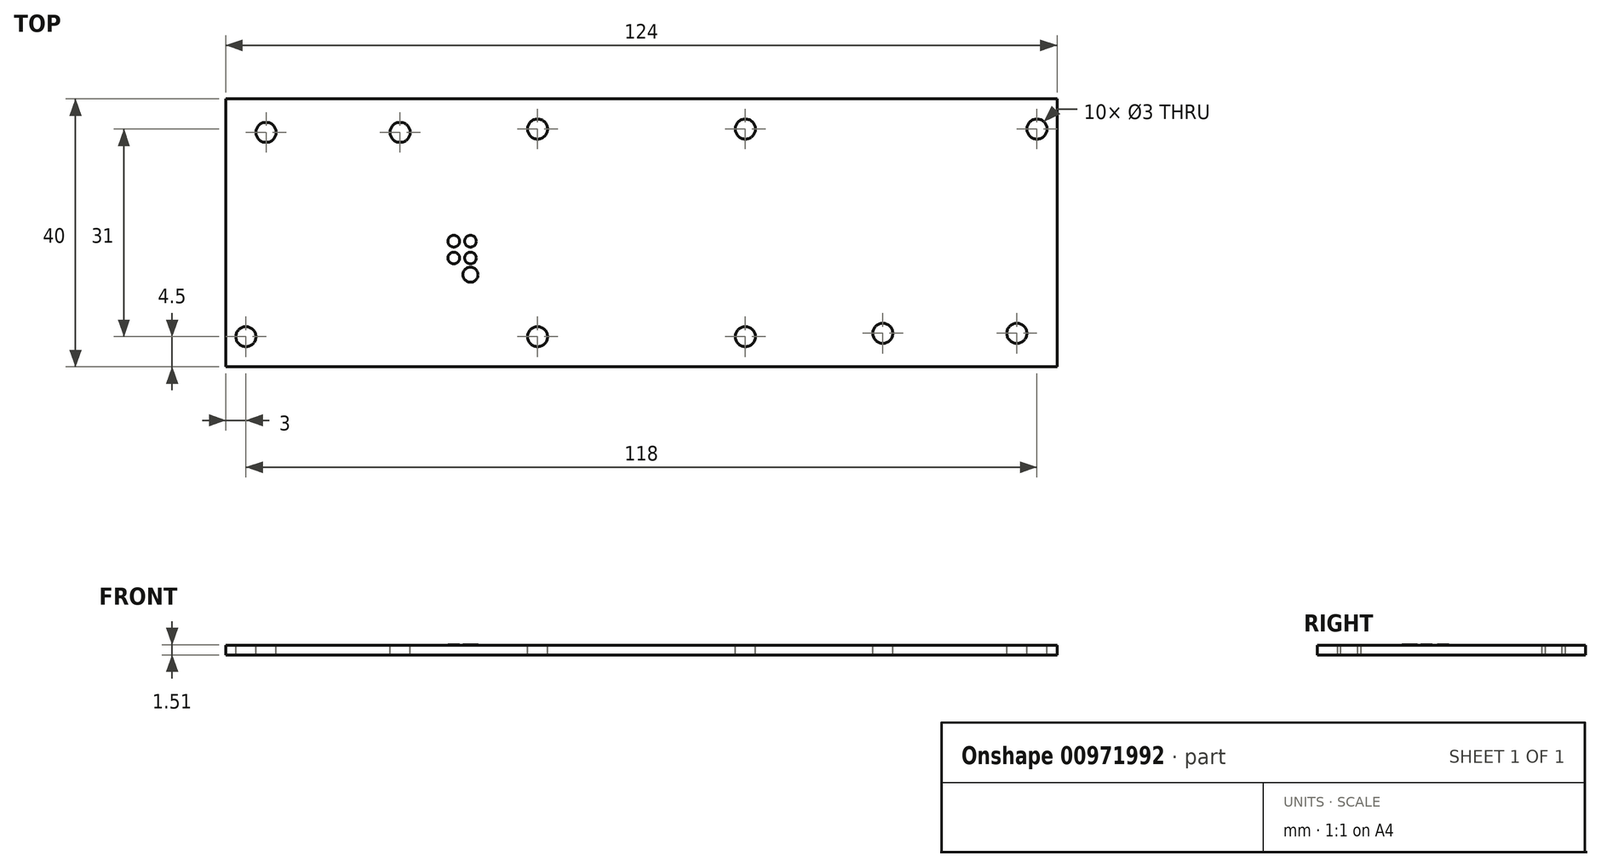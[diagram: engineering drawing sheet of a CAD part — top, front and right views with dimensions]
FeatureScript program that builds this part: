
annotation { "Feature Type Name" : "Feature", "Feature Type Description" : "" }
export const myFeature = defineFeature(function(context is Context, id is Id, definition is map)
    precondition{}
    {
        {
            var Q0;
            Q0=qCreatedBy(makeId("Top.planeOp"),FACE);
            var sketch = newSketch(context, id + "F0", { "sketchPlane" : qUnion([Q0])});
            skLineSegment(sketch, "E0.bottom", {"start": v(-62, 20) * mm, "end": v(62, 20) * mm});
            skLineSegment(sketch, "E0.top", {"start": v(-62, -20) * mm, "end": v(62, -20) * mm});
            skLineSegment(sketch, "E0.left", {"start": v(-62, 20) * mm, "end": v(-62, -20) * mm});
            skLineSegment(sketch, "E0.right", {"start": v(62, 20) * mm, "end": v(62, -20) * mm});
            skPoint(sketch, "E0.middle", {"position": v(0, 0) * mm});
            skSolve(sketch);
        }
        {
            var Q0;
            Q0=makeQuery(id+"F0.imprint","IMPRINT",FACE,{"disambiguationData":[TD([[makeQuery(id+"F0.imprint","IMPRINT",EDGE,{"derivedFrom":sQuery(id+"F0.wireOp",EDGE,"E0.bottom")}),-1.0]])]});
            extrude(context, id + "F1", {"entities" : qUnion([Q0]), "depth" : 1.41 * mm, "offsetDistance" : 25 * mm});
        }
        {
            var Q0;
            Q0=makeQuery(id+"F1.opExtrude","CAP_FACE",FACE,{"disambiguationData":[OSD([sQuery(id+"F0.wireOp",EDGE,"E0.bottom"),sQuery(id+"F0.wireOp",EDGE,"E0.top"),sQuery(id+"F0.wireOp",EDGE,"E0.left"),sQuery(id+"F0.wireOp",EDGE,"E0.right")])],"isStart":false});
            var sketch = newSketch(context, id + "F2", { "sketchPlane" : qUnion([Q0])});
            skLineSegment(sketch, "E1.bottom", {"start": v(-62, 18.5) * mm, "end": v(62, 18.5) * mm});
            skLineSegment(sketch, "E1.top", {"start": v(-62, -18.5) * mm, "end": v(62, -18.5) * mm});
            skLineSegment(sketch, "E1.left", {"start": v(-62, 18.5) * mm, "end": v(-62, -18.5) * mm});
            skLineSegment(sketch, "E1.right", {"start": v(62, 18.5) * mm, "end": v(62, -18.5) * mm});
            skPoint(sketch, "E1.middle", {"position": v(0, 0) * mm});
            skLineSegment(sketch, "E2.bottom", {"start": v(-62, -18.5) * mm, "end": v(-59, -18.5) * mm});
            skLineSegment(sketch, "E2.top", {"start": v(-62, -15.5) * mm, "end": v(-59, -15.5) * mm});
            skLineSegment(sketch, "E2.left", {"start": v(-62, -18.5) * mm, "end": v(-62, -15.5) * mm});
            skLineSegment(sketch, "E2.right", {"start": v(-59, -18.5) * mm, "end": v(-59, -15.5) * mm});
            skLineSegment(sketch, "E3.bottom", {"start": v(-62, 18.5) * mm, "end": v(-56, 18.5) * mm});
            skLineSegment(sketch, "E3.top", {"start": v(-62, 15) * mm, "end": v(-56, 15) * mm});
            skLineSegment(sketch, "E3.left", {"start": v(-62, 18.5) * mm, "end": v(-62, 15) * mm});
            skLineSegment(sketch, "E3.right", {"start": v(-56, 18.5) * mm, "end": v(-56, 15) * mm});
            skLineSegment(sketch, "E4", {"start": v(-59, -15.5) * mm, "end": v(-59, 15) * mm});
            skLineSegment(sketch, "E5", {"start": v(-56, 15) * mm, "end": v(-36, 15) * mm});
            skCircle(sketch, "E6", {"center": v(-56, 15) * mm, "radius": 1.5 * mm});
            skCircle(sketch, "E7", {"center": v(-59, -15.5) * mm, "radius": 1.5 * mm});
            skCircle(sketch, "E8", {"center": v(-36, 15) * mm, "radius": 1.5 * mm});
            skLineSegment(sketch, "E9.bottom", {"start": v(62, 18.5) * mm, "end": v(59, 18.5) * mm});
            skLineSegment(sketch, "E9.top", {"start": v(62, 15.5) * mm, "end": v(59, 15.5) * mm});
            skLineSegment(sketch, "E9.left", {"start": v(62, 18.5) * mm, "end": v(62, 15.5) * mm});
            skLineSegment(sketch, "E9.right", {"start": v(59, 18.5) * mm, "end": v(59, 15.5) * mm});
            skLineSegment(sketch, "E10", {"start": v(59, 15.5) * mm, "end": v(59, -15) * mm});
            skLineSegment(sketch, "E11", {"start": v(59, -15) * mm, "end": v(56, -15) * mm});
            skCircle(sketch, "E12", {"center": v(56, -15) * mm, "radius": 1.5 * mm});
            skLineSegment(sketch, "E13", {"start": v(56, -15) * mm, "end": v(36, -15) * mm});
            skCircle(sketch, "E14", {"center": v(36, -15) * mm, "radius": 1.5 * mm});
            skCircle(sketch, "E15", {"center": v(59, 15.5) * mm, "radius": 1.5 * mm});
            skSolve(sketch);
        }
        {
            var Q0;
            {var subQ0=sQuery(id+"F2.wireOp",EDGE,"E5");var subQ3=sQuery(id+"F2.wireOp",EDGE,"E6");var subQ5=makeQuery(id+"F2.imprint","INTERSECT",VERTEX,{"derivedFrom":[subQ0,subQ3]});Q0=makeQuery(id+"F2.imprint","IMPRINT",FACE,{"disambiguationData":[TD([[makeQuery(id+"F2.imprint","IMPRINT",EDGE,{"disambiguationData":[TD([[subQ5,1.0]])],"derivedFrom":subQ3}),1.0]])]});}
            var Q1;
            {var subQ1=sQuery(id+"F2.wireOp",EDGE,"E3.top");var subQ3=sQuery(id+"F2.wireOp",EDGE,"E6");var subQ4=makeQuery(id+"F2.imprint","INTERSECT",VERTEX,{"derivedFrom":[subQ1,subQ3]});Q1=makeQuery(id+"F2.imprint","IMPRINT",FACE,{"disambiguationData":[TD([[makeQuery(id+"F2.imprint","IMPRINT",EDGE,{"disambiguationData":[TD([[subQ4,1.0]])],"derivedFrom":subQ3}),1.0]])]});}
            var Q2;
            {var subQ0=sQuery(id+"F2.wireOp",EDGE,"E5");var subQ3=sQuery(id+"F2.wireOp",EDGE,"E6");var subQ5=makeQuery(id+"F2.imprint","INTERSECT",VERTEX,{"derivedFrom":[subQ0,subQ3]});Q2=makeQuery(id+"F2.imprint","IMPRINT",FACE,{"disambiguationData":[TD([[makeQuery(id+"F2.imprint","IMPRINT",EDGE,{"disambiguationData":[TD([[subQ5,-1.0]])],"derivedFrom":subQ3}),1.0]])]});}
            var Q3;
            Q3=makeQuery(id+"F2.imprint","IMPRINT",FACE,{"disambiguationData":[TD([[makeQuery(id+"F2.imprint","IMPRINT",EDGE,{"derivedFrom":sQuery(id+"F2.wireOp",EDGE,"E8")}),1.0]])]});
            var Q4;
            {var subQ1=sQuery(id+"F2.wireOp",EDGE,"E2.right");var subQ3=sQuery(id+"F2.wireOp",EDGE,"E7");var subQ4=makeQuery(id+"F2.imprint","INTERSECT",VERTEX,{"derivedFrom":[subQ1,subQ3]});Q4=makeQuery(id+"F2.imprint","IMPRINT",FACE,{"disambiguationData":[TD([[makeQuery(id+"F2.imprint","IMPRINT",EDGE,{"disambiguationData":[TD([[subQ4,-1.0]])],"derivedFrom":subQ3}),1.0]])]});}
            var Q5;
            {var subQ1=sQuery(id+"F2.wireOp",EDGE,"E2.top");var subQ3=sQuery(id+"F2.wireOp",EDGE,"E7");var subQ4=makeQuery(id+"F2.imprint","INTERSECT",VERTEX,{"derivedFrom":[subQ1,subQ3]});Q5=makeQuery(id+"F2.imprint","IMPRINT",FACE,{"disambiguationData":[TD([[makeQuery(id+"F2.imprint","IMPRINT",EDGE,{"disambiguationData":[TD([[subQ4,1.0]])],"derivedFrom":subQ3}),1.0]])]});}
            var Q6;
            {var subQ1=sQuery(id+"F2.wireOp",EDGE,"E2.top");var subQ3=sQuery(id+"F2.wireOp",EDGE,"E7");var subQ4=makeQuery(id+"F2.imprint","INTERSECT",VERTEX,{"derivedFrom":[subQ1,subQ3]});Q6=makeQuery(id+"F2.imprint","IMPRINT",FACE,{"disambiguationData":[TD([[makeQuery(id+"F2.imprint","IMPRINT",EDGE,{"disambiguationData":[TD([[subQ4,-1.0]])],"derivedFrom":subQ3}),1.0]])]});}
            var Q7;
            {var subQ1=sQuery(id+"F2.wireOp",EDGE,"E9.top");var subQ3=sQuery(id+"F2.wireOp",EDGE,"E15");var subQ4=makeQuery(id+"F2.imprint","INTERSECT",VERTEX,{"derivedFrom":[subQ1,subQ3]});Q7=makeQuery(id+"F2.imprint","IMPRINT",FACE,{"disambiguationData":[TD([[makeQuery(id+"F2.imprint","IMPRINT",EDGE,{"disambiguationData":[TD([[subQ4,-1.0]])],"derivedFrom":subQ3}),1.0]])]});}
            var Q8;
            {var subQ0=sQuery(id+"F2.wireOp",EDGE,"E10");var subQ3=sQuery(id+"F2.wireOp",EDGE,"E15");var subQ5=makeQuery(id+"F2.imprint","INTERSECT",VERTEX,{"derivedFrom":[subQ0,subQ3]});Q8=makeQuery(id+"F2.imprint","IMPRINT",FACE,{"disambiguationData":[TD([[makeQuery(id+"F2.imprint","IMPRINT",EDGE,{"disambiguationData":[TD([[subQ5,-1.0]])],"derivedFrom":subQ3}),1.0]])]});}
            var Q9;
            {var subQ0=sQuery(id+"F2.wireOp",EDGE,"E10");var subQ3=sQuery(id+"F2.wireOp",EDGE,"E15");var subQ5=makeQuery(id+"F2.imprint","INTERSECT",VERTEX,{"derivedFrom":[subQ0,subQ3]});Q9=makeQuery(id+"F2.imprint","IMPRINT",FACE,{"disambiguationData":[TD([[makeQuery(id+"F2.imprint","IMPRINT",EDGE,{"disambiguationData":[TD([[subQ5,1.0]])],"derivedFrom":subQ3}),1.0]])]});}
            var Q10;
            {var subQ0=sQuery(id+"F2.wireOp",EDGE,"E13");var subQ1=sQuery(id+"F2.wireOp",EDGE,"E11");var subQ2=makeQuery(id+"F2.imprint","INTERSECT",VERTEX,{"derivedFrom":[subQ1,subQ0]});Q10=makeQuery(id+"F2.imprint","IMPRINT",FACE,{"disambiguationData":[TD([[makeQuery(id+"F2.imprint","IMPRINT",EDGE,{"disambiguationData":[TD([[subQ2,1.0]])],"derivedFrom":subQ1}),1.0]])]});}
            var Q11;
            {var subQ0=sQuery(id+"F2.wireOp",EDGE,"E13");var subQ1=sQuery(id+"F2.wireOp",EDGE,"E11");var subQ2=makeQuery(id+"F2.imprint","INTERSECT",VERTEX,{"derivedFrom":[subQ1,subQ0]});Q11=makeQuery(id+"F2.imprint","IMPRINT",FACE,{"disambiguationData":[TD([[makeQuery(id+"F2.imprint","IMPRINT",EDGE,{"disambiguationData":[TD([[subQ2,1.0]])],"derivedFrom":subQ1}),-1.0]])]});}
            var Q12;
            Q12=makeQuery(id+"F2.imprint","IMPRINT",FACE,{"disambiguationData":[TD([[makeQuery(id+"F2.imprint","IMPRINT",EDGE,{"derivedFrom":sQuery(id+"F2.wireOp",EDGE,"E14")}),1.0]])]});
            extrude(context, id + "F3", {"entities" : qUnion([Q0, Q1, Q2, Q3, Q4, Q5, Q6, Q7, Q8, Q9, Q10, Q11, Q12]), "operationType" : NewBodyOperationType.REMOVE, "oppositeDirection" : true, "depth" : 25 * mm, "offsetDistance" : 25 * mm});
        }
        {
            var Q0;
            Q0=makeQuery(id+"F1.opExtrude","CAP_FACE",FACE,{"disambiguationData":[OSD([sQuery(id+"F0.wireOp",EDGE,"E0.bottom"),sQuery(id+"F0.wireOp",EDGE,"E0.top"),sQuery(id+"F0.wireOp",EDGE,"E0.left"),sQuery(id+"F0.wireOp",EDGE,"E0.right")])],"isStart":false});
            var sketch = newSketch(context, id + "F4", { "sketchPlane" : qUnion([Q0])});
            skLineSegment(sketch, "E16.bottom", {"start": v(-15.5, 15.5) * mm, "end": v(15.5, 15.5) * mm});
            skLineSegment(sketch, "E16.top", {"start": v(-15.5, -15.5) * mm, "end": v(15.5, -15.5) * mm});
            skLineSegment(sketch, "E16.left", {"start": v(-15.5, 15.5) * mm, "end": v(-15.5, -15.5) * mm});
            skLineSegment(sketch, "E16.right", {"start": v(15.5, 15.5) * mm, "end": v(15.5, -15.5) * mm});
            skPoint(sketch, "E16.middle", {"position": v(0, 0) * mm});
            skCircle(sketch, "E17", {"center": v(-15.5, 15.5) * mm, "radius": 1.5 * mm});
            skCircle(sketch, "E18", {"center": v(15.5, 15.5) * mm, "radius": 1.5 * mm});
            skCircle(sketch, "E19", {"center": v(15.5, -15.5) * mm, "radius": 1.5 * mm});
            skCircle(sketch, "E20", {"center": v(-15.5, -15.5) * mm, "radius": 1.5 * mm});
            skSolve(sketch);
        }
        {
            var Q0;
            {var subQ0=sQuery(id+"F4.wireOp",EDGE,"E16.left");var subQ1=sQuery(id+"F4.wireOp",EDGE,"E16.bottom");var subQ2=makeQuery(id+"F4.imprint","INTERSECT",VERTEX,{"derivedFrom":[subQ1,subQ0]});Q0=makeQuery(id+"F4.imprint","IMPRINT",FACE,{"disambiguationData":[TD([[makeQuery(id+"F4.imprint","IMPRINT",EDGE,{"disambiguationData":[TD([[subQ2,-1.0]])],"derivedFrom":subQ1}),1.0]])]});}
            var Q1;
            {var subQ0=sQuery(id+"F4.wireOp",EDGE,"E16.left");var subQ1=sQuery(id+"F4.wireOp",EDGE,"E16.bottom");var subQ2=makeQuery(id+"F4.imprint","INTERSECT",VERTEX,{"derivedFrom":[subQ1,subQ0]});Q1=makeQuery(id+"F4.imprint","IMPRINT",FACE,{"disambiguationData":[TD([[makeQuery(id+"F4.imprint","IMPRINT",EDGE,{"disambiguationData":[TD([[subQ2,-1.0]])],"derivedFrom":subQ1}),-1.0]])]});}
            var Q2;
            {var subQ0=sQuery(id+"F4.wireOp",EDGE,"E16.right");var subQ1=sQuery(id+"F4.wireOp",EDGE,"E16.bottom");var subQ2=makeQuery(id+"F4.imprint","INTERSECT",VERTEX,{"derivedFrom":[subQ1,subQ0]});Q2=makeQuery(id+"F4.imprint","IMPRINT",FACE,{"disambiguationData":[TD([[makeQuery(id+"F4.imprint","IMPRINT",EDGE,{"disambiguationData":[TD([[subQ2,1.0]])],"derivedFrom":subQ1}),-1.0]])]});}
            var Q3;
            {var subQ0=sQuery(id+"F4.wireOp",EDGE,"E16.right");var subQ1=sQuery(id+"F4.wireOp",EDGE,"E16.bottom");var subQ2=makeQuery(id+"F4.imprint","INTERSECT",VERTEX,{"derivedFrom":[subQ1,subQ0]});Q3=makeQuery(id+"F4.imprint","IMPRINT",FACE,{"disambiguationData":[TD([[makeQuery(id+"F4.imprint","IMPRINT",EDGE,{"disambiguationData":[TD([[subQ2,1.0]])],"derivedFrom":subQ1}),1.0]])]});}
            var Q4;
            {var subQ0=sQuery(id+"F4.wireOp",EDGE,"E16.left");var subQ1=sQuery(id+"F4.wireOp",EDGE,"E16.top");var subQ2=makeQuery(id+"F4.imprint","INTERSECT",VERTEX,{"derivedFrom":[subQ1,subQ0]});Q4=makeQuery(id+"F4.imprint","IMPRINT",FACE,{"disambiguationData":[TD([[makeQuery(id+"F4.imprint","IMPRINT",EDGE,{"disambiguationData":[TD([[subQ2,-1.0]])],"derivedFrom":subQ1}),1.0]])]});}
            var Q5;
            {var subQ0=sQuery(id+"F4.wireOp",EDGE,"E16.left");var subQ1=sQuery(id+"F4.wireOp",EDGE,"E16.top");var subQ2=makeQuery(id+"F4.imprint","INTERSECT",VERTEX,{"derivedFrom":[subQ1,subQ0]});Q5=makeQuery(id+"F4.imprint","IMPRINT",FACE,{"disambiguationData":[TD([[makeQuery(id+"F4.imprint","IMPRINT",EDGE,{"disambiguationData":[TD([[subQ2,-1.0]])],"derivedFrom":subQ1}),-1.0]])]});}
            var Q6;
            {var subQ0=sQuery(id+"F4.wireOp",EDGE,"E16.right");var subQ1=sQuery(id+"F4.wireOp",EDGE,"E16.top");var subQ2=makeQuery(id+"F4.imprint","INTERSECT",VERTEX,{"derivedFrom":[subQ1,subQ0]});Q6=makeQuery(id+"F4.imprint","IMPRINT",FACE,{"disambiguationData":[TD([[makeQuery(id+"F4.imprint","IMPRINT",EDGE,{"disambiguationData":[TD([[subQ2,1.0]])],"derivedFrom":subQ1}),1.0]])]});}
            var Q7;
            {var subQ0=sQuery(id+"F4.wireOp",EDGE,"E16.right");var subQ1=sQuery(id+"F4.wireOp",EDGE,"E16.top");var subQ2=makeQuery(id+"F4.imprint","INTERSECT",VERTEX,{"derivedFrom":[subQ1,subQ0]});Q7=makeQuery(id+"F4.imprint","IMPRINT",FACE,{"disambiguationData":[TD([[makeQuery(id+"F4.imprint","IMPRINT",EDGE,{"disambiguationData":[TD([[subQ2,1.0]])],"derivedFrom":subQ1}),-1.0]])]});}
            extrude(context, id + "F5", {"entities" : qUnion([Q0, Q1, Q2, Q3, Q4, Q5, Q6, Q7]), "operationType" : NewBodyOperationType.REMOVE, "oppositeDirection" : true, "depth" : 25 * mm, "offsetDistance" : 25 * mm});
        }
        {
            var Q0;
            Q0=makeQuery(id+"F1.opExtrude","CAP_FACE",FACE,{"disambiguationData":[OSD([sQuery(id+"F0.wireOp",EDGE,"E0.bottom"),sQuery(id+"F0.wireOp",EDGE,"E0.top"),sQuery(id+"F0.wireOp",EDGE,"E0.left"),sQuery(id+"F0.wireOp",EDGE,"E0.right")])],"isStart":false});
            var sketch = newSketch(context, id + "F6", { "sketchPlane" : qUnion([Q0])});
            skLineSegment(sketch, "E21", {"start": v(-62, -20) * mm, "end": v(-25.5, -20) * mm});
            skLineSegment(sketch, "E22", {"start": v(-25.5, -20) * mm, "end": v(-25.5, -6.25) * mm});
            skCircle(sketch, "E23", {"center": v(-25.5, -6.25) * mm, "radius": 1.13 * mm});
            skLineSegment(sketch, "E24", {"start": v(-25.5, -6.25) * mm, "end": v(-25.5, -3.75) * mm});
            skCircle(sketch, "E25", {"center": v(-25.5, -3.75) * mm, "radius": 0.88 * mm});
            skLineSegment(sketch, "E26", {"start": v(-25.5, -3.75) * mm, "end": v(-25.5, -1.25) * mm});
            skCircle(sketch, "E27", {"center": v(-25.5, -1.25) * mm, "radius": 0.88 * mm});
            skLineSegment(sketch, "E28.0", {"start": v(-62, 20) * mm, "end": v(-62, -20) * mm});
            skLineSegment(sketch, "E29", {"start": v(0, 0) * mm, "end": v(0, -18.5) * mm});
            skLineSegment(sketch, "E30", {"start": v(-25.5, -1.25) * mm, "end": v(-25.5, 1.25) * mm});
            skCircle(sketch, "E31", {"center": v(-25.5, 1.25) * mm, "radius": 1.13 * mm});
            skLineSegment(sketch, "E32", {"start": v(-25.5, 0.13) * mm, "end": v(-25.5, 1.25) * mm});
            skLineSegment(sketch, "E33", {"start": v(-20.67, 18.5) * mm, "end": v(-25.5, 18.5) * mm});
            skLineSegment(sketch, "E34", {"start": v(-25.5, 18.5) * mm, "end": v(-25.5, 18.38) * mm});
            skLineSegment(sketch, "E35.bottom", {"start": v(-25.5, -18.5) * mm, "end": v(25.5, -18.5) * mm});
            skLineSegment(sketch, "E35.top", {"start": v(-25.5, 18.5) * mm, "end": v(25.5, 18.5) * mm});
            skLineSegment(sketch, "E35.left", {"start": v(-25.5, -18.5) * mm, "end": v(-25.5, 18.5) * mm});
            skLineSegment(sketch, "E35.right", {"start": v(25.5, -18.5) * mm, "end": v(25.5, 18.5) * mm});
            skPoint(sketch, "E35.middle", {"position": v(0, 0) * mm});
            skLineSegment(sketch, "E36", {"start": v(-25.5, -1.25) * mm, "end": v(-28, -1.25) * mm});
            skCircle(sketch, "E37", {"center": v(-28, -1.25) * mm, "radius": 0.88 * mm});
            skCircle(sketch, "E38", {"center": v(-28, -3.75) * mm, "radius": 0.88 * mm});
            skLineSegment(sketch, "E39.trimOffspring", {"start": v(-25.5, 2.38) * mm, "end": v(-25.5, 18.38) * mm});
            skSolve(sketch);
        }
        {
            var Q0;
            Q0=makeQuery(id+"F6.imprint","IMPRINT",FACE,{"disambiguationData":[TD([[makeQuery(id+"F6.imprint","IMPRINT",EDGE,{"derivedFrom":sQuery(id+"F6.wireOp",EDGE,"E37")}),1.0]])]});
            var Q1;
            Q1=makeQuery(id+"F6.imprint","IMPRINT",FACE,{"disambiguationData":[TD([[makeQuery(id+"F6.imprint","IMPRINT",EDGE,{"derivedFrom":sQuery(id+"F6.wireOp",EDGE,"E38")}),1.0]])]});
            var Q2;
            {var subQ0=sQuery(id+"F6.wireOp",EDGE,"E35.left");var subQ1=sQuery(id+"F6.wireOp",EDGE,"E23");var subQ2=makeQuery(id+"F6.imprint","INTERSECT",VERTEX,{"disambiguationData":[OD(0.0)],"derivedFrom":[subQ1,subQ0]});Q2=makeQuery(id+"F6.imprint","IMPRINT",FACE,{"disambiguationData":[TD([[makeQuery(id+"F6.imprint","IMPRINT",EDGE,{"disambiguationData":[TD([[subQ2,1.0]])],"derivedFrom":subQ1}),1.0]])]});}
            var Q3;
            {var subQ0=sQuery(id+"F6.wireOp",EDGE,"E35.left");var subQ1=sQuery(id+"F6.wireOp",EDGE,"E23");var subQ2=makeQuery(id+"F6.imprint","INTERSECT",VERTEX,{"disambiguationData":[OD(0.0)],"derivedFrom":[subQ1,subQ0]});Q3=makeQuery(id+"F6.imprint","IMPRINT",FACE,{"disambiguationData":[TD([[makeQuery(id+"F6.imprint","IMPRINT",EDGE,{"disambiguationData":[TD([[subQ2,-1.0]])],"derivedFrom":subQ1}),1.0]])]});}
            var Q4;
            {var subQ0=sQuery(id+"F6.wireOp",EDGE,"E35.left");var subQ1=sQuery(id+"F6.wireOp",EDGE,"E25");var subQ2=makeQuery(id+"F6.imprint","INTERSECT",VERTEX,{"disambiguationData":[OD(0.0)],"derivedFrom":[subQ1,subQ0]});Q4=makeQuery(id+"F6.imprint","IMPRINT",FACE,{"disambiguationData":[TD([[makeQuery(id+"F6.imprint","IMPRINT",EDGE,{"disambiguationData":[TD([[subQ2,1.0]])],"derivedFrom":subQ1}),1.0]])]});}
            var Q5;
            {var subQ0=sQuery(id+"F6.wireOp",EDGE,"E35.left");var subQ1=sQuery(id+"F6.wireOp",EDGE,"E25");var subQ2=makeQuery(id+"F6.imprint","INTERSECT",VERTEX,{"disambiguationData":[OD(0.0)],"derivedFrom":[subQ1,subQ0]});Q5=makeQuery(id+"F6.imprint","IMPRINT",FACE,{"disambiguationData":[TD([[makeQuery(id+"F6.imprint","IMPRINT",EDGE,{"disambiguationData":[TD([[subQ2,-1.0]])],"derivedFrom":subQ1}),1.0]])]});}
            var Q6;
            {var subQ0=sQuery(id+"F6.wireOp",EDGE,"E35.left");var subQ4=makeQuery(id+"F6.imprint","IMPRINT",VERTEX,{"derivedFrom":subQ0});Q6=makeQuery(id+"F6.imprint","IMPRINT",FACE,{"disambiguationData":[TD([[makeQuery(id+"F6.imprint","IMPRINT",EDGE,{"disambiguationData":[TD([[subQ4,1.0]])],"derivedFrom":subQ0}),1.0]])]});}
            var Q7;
            {var subQ0=sQuery(id+"F6.wireOp",EDGE,"E35.left");var subQ4=makeQuery(id+"F6.imprint","IMPRINT",VERTEX,{"derivedFrom":subQ0});Q7=makeQuery(id+"F6.imprint","IMPRINT",FACE,{"disambiguationData":[TD([[makeQuery(id+"F6.imprint","IMPRINT",EDGE,{"disambiguationData":[TD([[subQ4,1.0]])],"derivedFrom":subQ0}),-1.0]])]});}
            var Q8;
            {var subQ0=sQuery(id+"F6.wireOp",EDGE,"E36");var subQ1=sQuery(id+"F6.wireOp",EDGE,"E27");var subQ2=makeQuery(id+"F6.imprint","INTERSECT",VERTEX,{"derivedFrom":[subQ1,subQ0]});Q8=makeQuery(id+"F6.imprint","IMPRINT",FACE,{"disambiguationData":[TD([[makeQuery(id+"F6.imprint","IMPRINT",EDGE,{"disambiguationData":[TD([[subQ2,1.0]])],"derivedFrom":subQ1}),1.0]])]});}
            var Q9;
            {var subQ0=sQuery(id+"F6.wireOp",EDGE,"E36");var subQ1=sQuery(id+"F6.wireOp",EDGE,"E27");var subQ2=makeQuery(id+"F6.imprint","INTERSECT",VERTEX,{"derivedFrom":[subQ1,subQ0]});Q9=makeQuery(id+"F6.imprint","IMPRINT",FACE,{"disambiguationData":[TD([[makeQuery(id+"F6.imprint","IMPRINT",EDGE,{"disambiguationData":[TD([[subQ2,-1.0]])],"derivedFrom":subQ1}),1.0]])]});}
            var Q10;
            {var subQ0=sQuery(id+"F6.wireOp",EDGE,"E35.left");var subQ1=sQuery(id+"F6.wireOp",EDGE,"E27");var subQ2=makeQuery(id+"F6.imprint","INTERSECT",VERTEX,{"disambiguationData":[OD(0.0)],"derivedFrom":[subQ1,subQ0]});Q10=makeQuery(id+"F6.imprint","IMPRINT",FACE,{"disambiguationData":[TD([[makeQuery(id+"F6.imprint","IMPRINT",EDGE,{"disambiguationData":[TD([[subQ2,1.0]])],"derivedFrom":subQ1}),1.0]])]});}
            extrude(context, id + "F7", {"entities" : qUnion([Q0, Q1, Q2, Q3, Q4, Q5, Q6, Q7, Q8, Q9, Q10]), "operationType" : NewBodyOperationType.ADD, "depth" : .1 * mm, "offsetDistance" : 25 * mm});
        }
        {
            var Q0;
            Q0=qCreatedBy(makeId("Front.planeOp"),FACE);
            var sketch = newSketch(context, id + "F8", { "sketchPlane" : qUnion([Q0])});
            skLineSegment(sketch, "E40", {"start": v(0, 0) * mm, "end": v(0, 12.05) * mm});
            skSolve(sketch);
        }
    });
